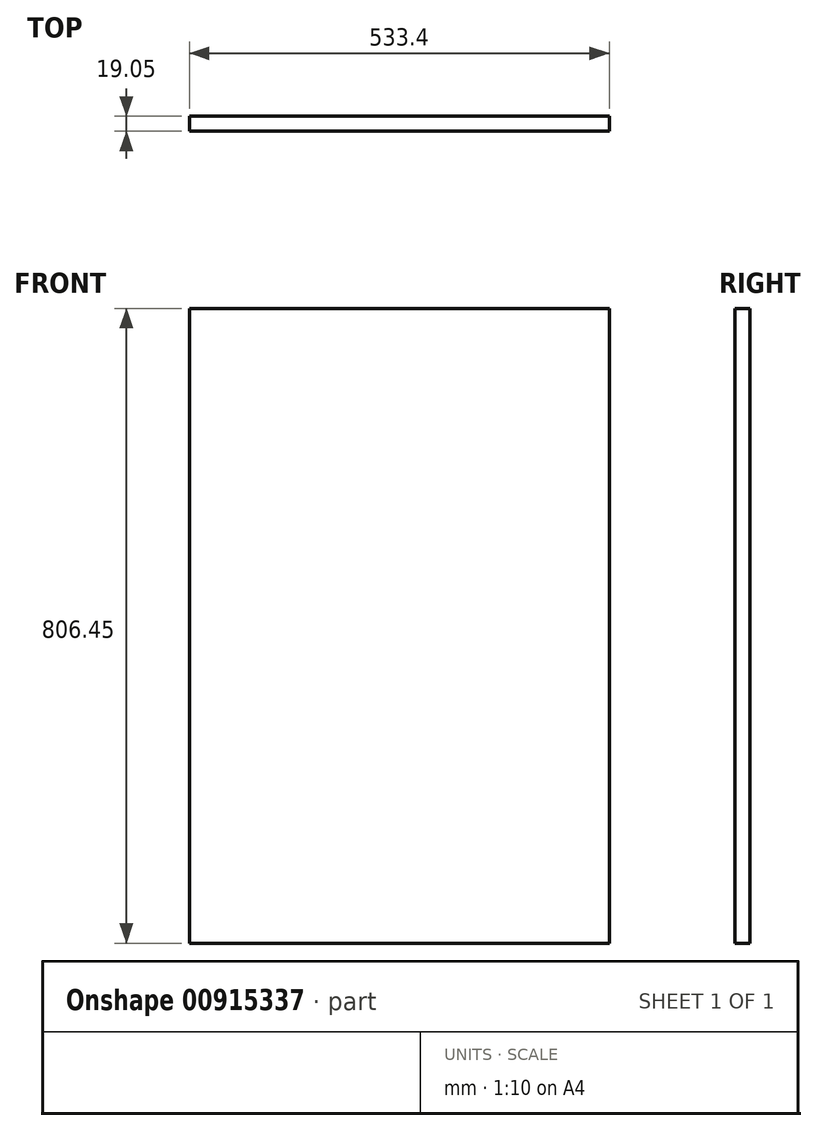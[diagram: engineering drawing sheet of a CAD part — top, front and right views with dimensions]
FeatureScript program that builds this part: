
annotation { "Feature Type Name" : "Feature", "Feature Type Description" : "" }
export const myFeature = defineFeature(function(context is Context, id is Id, definition is map)
    precondition{}
    {
        {
            var Q0;
            Q0=qCreatedBy(makeId("Front.planeOp"),FACE);
            var sketch = newSketch(context, id + "F0", { "sketchPlane" : qUnion([Q0])});
            skLineSegment(sketch, "E0.bottom", {"start": v(0, 0) * mm, "end": v(533.4, 0) * mm});
            skLineSegment(sketch, "E0.top", {"start": v(0, 806.45) * mm, "end": v(533.4, 806.45) * mm});
            skLineSegment(sketch, "E0.left", {"start": v(0, 0) * mm, "end": v(0, 806.45) * mm});
            skLineSegment(sketch, "E0.right", {"start": v(533.4, 0) * mm, "end": v(533.4, 806.45) * mm});
            skSolve(sketch);
        }
        {
            var Q0;
            Q0 = qSketchRegion(id + "F0", true);
            extrude(context, id + "F1", {"entities" : qUnion([Q0]), "depth" : 19.05 * mm, "offsetDistance" : 25.4 * mm});
        }
    });
